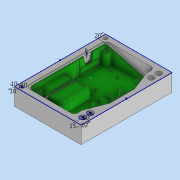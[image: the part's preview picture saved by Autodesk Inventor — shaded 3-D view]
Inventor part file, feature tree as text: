
AUTODESK INVENTOR PART (.ipt)
format: ipt  version: 2022 (Build 260153070, 153G)  size: 2,766,336 bytes
history: native  units: mm
features: other x23, sketch x13, surface_op x8, extrude x7, plane x6, revolve x5, mirror x2, boolean_combine x2, thicken_offset x2, split x1, fillet x1, projected_geometry x1
ambient origin geometry x8: Origin, YZ Plane, XZ Plane, XY Plane, X Axis, Y Axis, Z Axis, Center Point
bodies: Solid2 (feature_tree), Solid3 (feature_tree), Solid4 (feature_tree), Solid6 (feature_tree)
feature tree (71):
  other  "P00173-09-004.ipt"
  other  "Blocks"
  sketch  "Sketch3"  dims[d0=10.0mm d1=2.0mm]
  sketch  "Sketch6"  dims[d2=3.5mm d3=20.0mm]
  plane  "Work Plane2"
  sketch  "Sketch9"  dims[d4=20.0mm d10=20.0mm]
  sketch  "Sketch21"  dims[d68=10.0mm d69=10.0mm d70=10.0mm]
  sketch  "Sketch17"  dims[d24=360.0deg d25=90.0deg d28=5.0mm]
  plane  "Work Plane4"
  surface_op  "Trim2"
  sketch  "Sketch11"  dims[d16=20.0mm d17=65.0mm]
  sketch  "Sketch14"  dims[d20=77.5mm d21=0.0mm d22=10.0mm d23=0.0mm]
  plane  "Work Plane6"
  surface_op  "Stitch Surface4"
  surface_op  "Trim5"
  surface_op  "Stitch Surface5"
  revolve  "Revolution1"  [1 undecoded]
  revolve  "Revolution2"  [1 undecoded]
  split  "Split1"
  mirror  "Mirror2"
  boolean_combine  "Combine1"
  boolean_combine  "Combine3"
  extrude  "Extrusion2"  Depth=20.0mm
  extrude  "Extrusion3"  Depth=10.0mm
  revolve  "Revolution3"  [1 undecoded]
  revolve  "Revolution4"  [1 undecoded]
  revolve  "Revolution5"  [1 undecoded]
  mirror  "Mirror3"
  extrude  "Extrusion4"  TaperAngle=90.0deg  [1 undecoded]
  fillet  "Fillet1"  Radius=5.0mm
  thicken_offset  "Thicken17"
  thicken_offset  "Thicken18"
  extrude  "Extrusion5"  Depth=40.0mm TaperAngle=0.0deg
  other  "Side"
  other  "Bottom"
  other  "Srf1"
  other  "Front_Vent_Holes"
  sketch  "Sketch69"  dims[d73=90.0deg d74=90.0deg d75=6.0mm d76=0.174533mm d77=2.0mm d80=0.2mm d81=0.2mm d82=0.2mm d83=0.2mm d84=0.0mm d85=0.0mm d29=0.872665mm d30=0.5mm d31=0.872665mm]
  plane  "Work Plane - Front_Vent_Holes"
  plane  "Work Plane - Parting Line"
  other  "Srf8"
  other  "Srf9"
  sketch  "Sketch10"  dims[d11=10.0mm d12=0.0mm d13=5.0mm]
  other  "Srf10"
  other  "Srf11"
  sketch  "Sketch13"  dims[d18=10.0mm d19=10.0mm]
  other  "Srf13"
  other  "Srf14"
  other  "Srf15"
  other  "Srf16"
  sketch  "Sketch33"  dims[d71=20.0mm d72=90.0deg]
  other  "Rear_Air_Hole_Strip"
  plane  "Work Plane - Rear_Air_Hole"
  other  "TaggingFeature2"
  other  "Solid6::P00173-09-004.ipt"
  sketch  "Sketch18"  dims[d61=2.0mm d62=0.0mm d63=40.0mm d64=0.0mm]
  other  "Power_Con_3"
  sketch  "Sketch20"  dims[d65=15.0mm d66=15.0mm d67=20.0mm]
  other  "Block1"
  other  "USB_Cable_Opening"
  other  "Srf16::Derived"
  extrude  "ExtrusionSrf4"  Depth=20.0mm
  extrude  "ExtrusionSrf6"  Depth=10.0mm
  extrude  "ExtrusionSrf7"  TaperAngle=90.0deg  [1 undecoded]
  projected_geometry  "Project Cut Edges1"
  other  "Block1:1"
  other  "Block1:2"
  surface_op  "Boundary Patch4"
  surface_op  "Boundary Patch3"
  surface_op  "Boundary Patch1"
  surface_op  "Boundary Patch2"
note: 7 required parameter values undecoded (feature->parameter linkage not recoverable at this tier; creation-order binding heuristic only, values carry confidence <= 0.55)